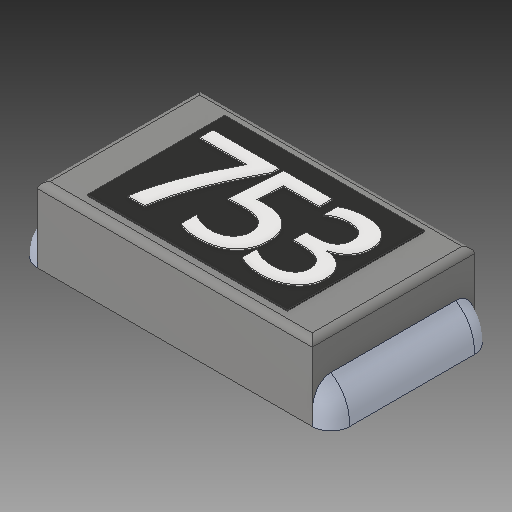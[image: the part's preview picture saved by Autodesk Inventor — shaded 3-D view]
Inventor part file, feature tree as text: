
AUTODESK INVENTOR PART (.ipt)
format: ipt  version: 2018.3 (Build 223284000, 284)  size: 260,096 bytes
history: native  units: mm
features: other x4, fillet x1, mirror x1
ambient origin geometry x8: Origin, YZ Plane, XZ Plane, XY Plane, X Axis, Y Axis, Z Axis, Center Point
bodies: Body1 (feature_tree), Body2 (feature_tree), Body3 (feature_tree)
feature tree (6):
  other  "Sólido1"
  other  "Sólido2"
  other  "Sólido3"
  fillet  "Fillet2"  [1 undecoded]
  mirror  "Mirror1"
  other  "Boss-Extrude4"
note: 1 required parameter value undecoded (feature->parameter linkage not recoverable at this tier; creation-order binding heuristic only, values carry confidence <= 0.55)
